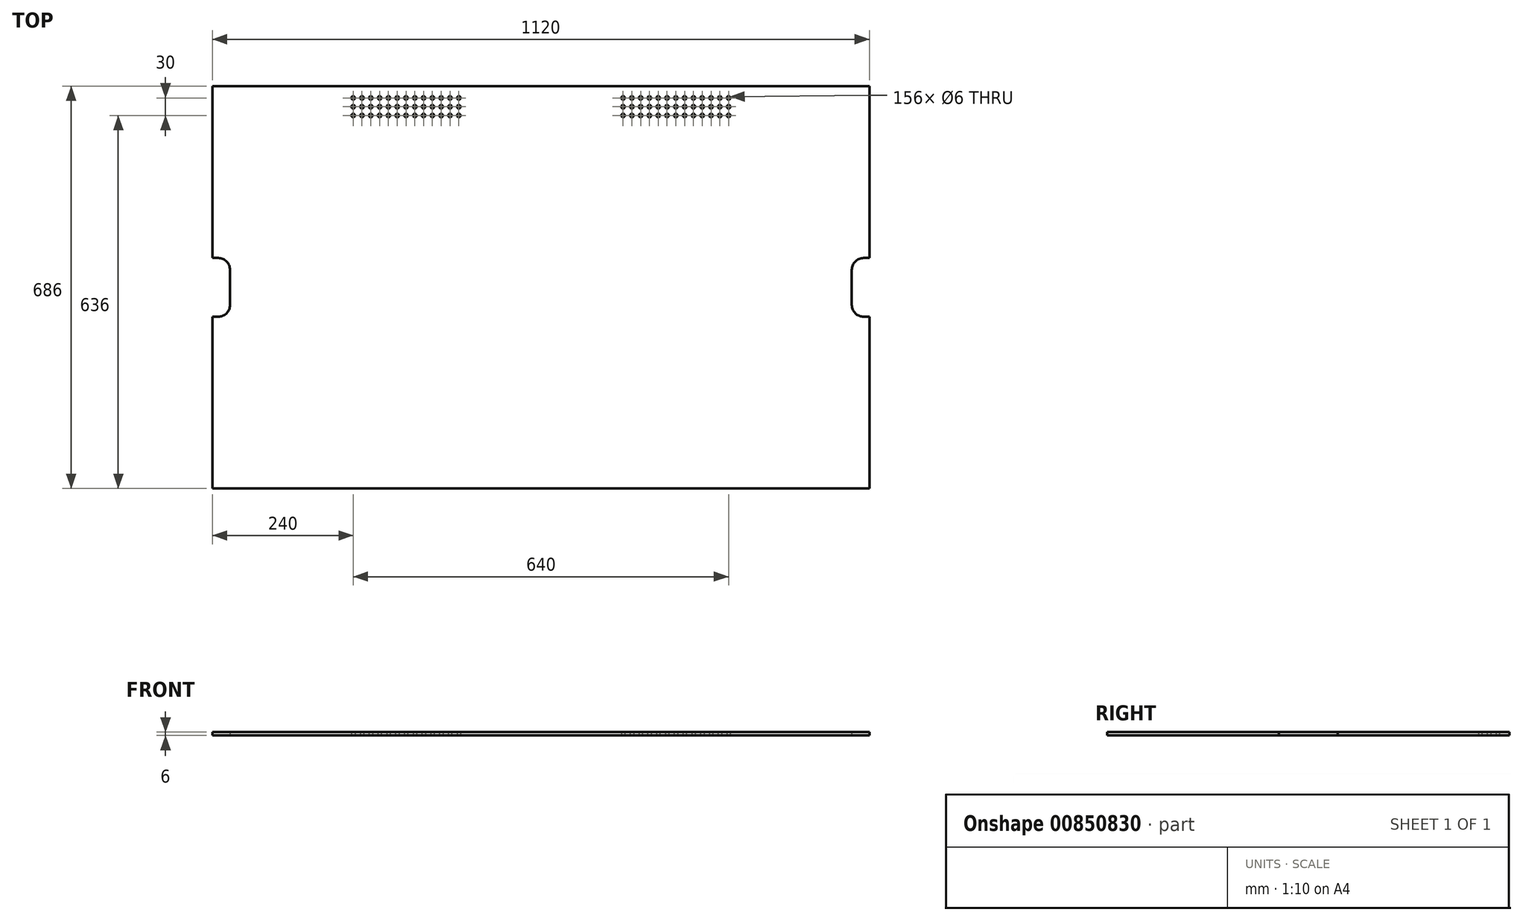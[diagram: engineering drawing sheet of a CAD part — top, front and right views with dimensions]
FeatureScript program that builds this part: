
annotation { "Feature Type Name" : "Feature", "Feature Type Description" : "" }
export const myFeature = defineFeature(function(context is Context, id is Id, definition is map)
    precondition{}
    {
        {
            var Q0;
            Q0=qCreatedBy(makeId("Top.planeOp"),FACE);
            var sketch = newSketch(context, id + "F0", { "sketchPlane" : qUnion([Q0])});
            skLineSegment(sketch, "E0", {"start": v(-560, 343) * mm, "end": v(-560, 50) * mm});
            skLineSegment(sketch, "E1", {"start": v(-560, 50) * mm, "end": v(-550, 50) * mm});
            skArc(sketch, "E2", {"start": v(-550, 50) * mm, "mid": v(-535.86, 44.14) * mm, "end": v(-530, 30) * mm});
            skLineSegment(sketch, "E3", {"start": v(-530, 30) * mm, "end": v(-530, -30) * mm});
            skArc(sketch, "E4", {"start": v(-530, -30) * mm, "mid": v(-535.86, -44.14) * mm, "end": v(-550, -50) * mm});
            skLineSegment(sketch, "E5", {"start": v(-550, -50) * mm, "end": v(-560, -50) * mm});
            skLineSegment(sketch, "E6", {"start": v(-560, -50) * mm, "end": v(-560, -343) * mm});
            skCircle(sketch, "E7", {"center": v(-140, 323) * mm, "radius": 3 * mm});
            skCircle(sketch, "E8.0.1.0", {"center": v(-140, 308) * mm, "radius": 3 * mm});
            skCircle(sketch, "E8.0.2.0", {"center": v(-140, 293) * mm, "radius": 3 * mm});
            skCircle(sketch, "E8.1.0.0", {"center": v(-155, 323) * mm, "radius": 3 * mm});
            skCircle(sketch, "E8.1.1.0", {"center": v(-155, 308) * mm, "radius": 3 * mm});
            skCircle(sketch, "E8.1.2.0", {"center": v(-155, 293) * mm, "radius": 3 * mm});
            skCircle(sketch, "E8.2.0.0", {"center": v(-170, 323) * mm, "radius": 3 * mm});
            skCircle(sketch, "E8.2.1.0", {"center": v(-170, 308) * mm, "radius": 3 * mm});
            skCircle(sketch, "E8.2.2.0", {"center": v(-170, 293) * mm, "radius": 3 * mm});
            skCircle(sketch, "E8.3.0.0", {"center": v(-185, 323) * mm, "radius": 3 * mm});
            skCircle(sketch, "E8.3.1.0", {"center": v(-185, 308) * mm, "radius": 3 * mm});
            skCircle(sketch, "E8.3.2.0", {"center": v(-185, 293) * mm, "radius": 3 * mm});
            skCircle(sketch, "E8.4.0.0", {"center": v(-200, 323) * mm, "radius": 3 * mm});
            skCircle(sketch, "E8.4.1.0", {"center": v(-200, 308) * mm, "radius": 3 * mm});
            skCircle(sketch, "E8.4.2.0", {"center": v(-200, 293) * mm, "radius": 3 * mm});
            skCircle(sketch, "E8.5.0.0", {"center": v(-215, 323) * mm, "radius": 3 * mm});
            skCircle(sketch, "E8.5.1.0", {"center": v(-215, 308) * mm, "radius": 3 * mm});
            skCircle(sketch, "E8.5.2.0", {"center": v(-215, 293) * mm, "radius": 3 * mm});
            skCircle(sketch, "E8.6.0.0", {"center": v(-230, 323) * mm, "radius": 3 * mm});
            skCircle(sketch, "E8.6.1.0", {"center": v(-230, 308) * mm, "radius": 3 * mm});
            skCircle(sketch, "E8.6.2.0", {"center": v(-230, 293) * mm, "radius": 3 * mm});
            skCircle(sketch, "E8.7.0.0", {"center": v(-245, 323) * mm, "radius": 3 * mm});
            skCircle(sketch, "E8.7.1.0", {"center": v(-245, 308) * mm, "radius": 3 * mm});
            skCircle(sketch, "E8.7.2.0", {"center": v(-245, 293) * mm, "radius": 3 * mm});
            skCircle(sketch, "E8.8.0.0", {"center": v(-260, 323) * mm, "radius": 3 * mm});
            skCircle(sketch, "E8.8.1.0", {"center": v(-260, 308) * mm, "radius": 3 * mm});
            skCircle(sketch, "E8.8.2.0", {"center": v(-260, 293) * mm, "radius": 3 * mm});
            skCircle(sketch, "E8.9.0.0", {"center": v(-275, 323) * mm, "radius": 3 * mm});
            skCircle(sketch, "E8.9.1.0", {"center": v(-275, 308) * mm, "radius": 3 * mm});
            skCircle(sketch, "E8.9.2.0", {"center": v(-275, 293) * mm, "radius": 3 * mm});
            skCircle(sketch, "E8.10.0.0", {"center": v(-290, 323) * mm, "radius": 3 * mm});
            skCircle(sketch, "E8.10.1.0", {"center": v(-290, 308) * mm, "radius": 3 * mm});
            skCircle(sketch, "E8.10.2.0", {"center": v(-290, 293) * mm, "radius": 3 * mm});
            skCircle(sketch, "E8.11.0.0", {"center": v(-305, 323) * mm, "radius": 3 * mm});
            skCircle(sketch, "E8.11.1.0", {"center": v(-305, 308) * mm, "radius": 3 * mm});
            skCircle(sketch, "E8.11.2.0", {"center": v(-305, 293) * mm, "radius": 3 * mm});
            skCircle(sketch, "E8.12.0.0", {"center": v(-320, 323) * mm, "radius": 3 * mm});
            skCircle(sketch, "E8.12.1.0", {"center": v(-320, 308) * mm, "radius": 3 * mm});
            skCircle(sketch, "E8.12.2.0", {"center": v(-320, 293) * mm, "radius": 3 * mm});
            skLineSegment(sketch, "E8.direction1", {"start": v(-140, 323) * mm, "end": v(-155, 323) * mm, "construction": true});
            skLineSegment(sketch, "E8.direction2", {"start": v(-140, 323) * mm, "end": v(-140, 308) * mm, "construction": true});
            skLineSegment(sketch, "E9", {"start": v(-560, 343) * mm, "end": v(0, 343) * mm});
            skLineSegment(sketch, "E10", {"start": v(-560, -343) * mm, "end": v(0, -343) * mm});
            skLineSegment(sketch, "E11", {"start": v(-612.39, 0) * mm, "end": v(606.49, 0) * mm, "construction": true});
            skLineSegment(sketch, "E12", {"start": v(0, 429.06) * mm, "end": v(0, -433.74) * mm, "construction": true});
            skLineSegment(sketch, "E13.MirrorCS", {"start": v(560, 343) * mm, "end": v(0, 343) * mm});
            skLineSegment(sketch, "E14.MirrorCS", {"start": v(560, 343) * mm, "end": v(560, 50) * mm});
            skLineSegment(sketch, "E15.MirrorCS", {"start": v(560, 50) * mm, "end": v(550, 50) * mm});
            skArc(sketch, "E16.MirrorCS", {"start": v(550, 50) * mm, "mid": v(535.86, 44.14) * mm, "end": v(530, 30) * mm});
            skLineSegment(sketch, "E17.MirrorCS", {"start": v(530, 30) * mm, "end": v(530, -30) * mm});
            skArc(sketch, "E18.MirrorCS", {"start": v(530, -30) * mm, "mid": v(535.86, -44.14) * mm, "end": v(550, -50) * mm});
            skLineSegment(sketch, "E19.MirrorCS", {"start": v(550, -50) * mm, "end": v(560, -50) * mm});
            skLineSegment(sketch, "E20.MirrorCS", {"start": v(560, -50) * mm, "end": v(560, -343) * mm});
            skLineSegment(sketch, "E21.MirrorCS", {"start": v(560, -343) * mm, "end": v(0, -343) * mm});
            skCircle(sketch, "E22.MirrorC", {"center": v(140, 323) * mm, "radius": 3 * mm});
            skCircle(sketch, "E23.MirrorC", {"center": v(155, 323) * mm, "radius": 3 * mm});
            skCircle(sketch, "E24.MirrorC", {"center": v(170, 323) * mm, "radius": 3 * mm});
            skCircle(sketch, "E25.MirrorC", {"center": v(185, 323) * mm, "radius": 3 * mm});
            skCircle(sketch, "E26.MirrorC", {"center": v(200, 323) * mm, "radius": 3 * mm});
            skCircle(sketch, "E27.MirrorC", {"center": v(215, 323) * mm, "radius": 3 * mm});
            skCircle(sketch, "E28.MirrorC", {"center": v(230, 323) * mm, "radius": 3 * mm});
            skCircle(sketch, "E29.MirrorC", {"center": v(245, 323) * mm, "radius": 3 * mm});
            skCircle(sketch, "E30.MirrorC", {"center": v(260, 323) * mm, "radius": 3 * mm});
            skCircle(sketch, "E31.MirrorC", {"center": v(275, 323) * mm, "radius": 3 * mm});
            skCircle(sketch, "E32.MirrorC", {"center": v(290, 323) * mm, "radius": 3 * mm});
            skCircle(sketch, "E33.MirrorC", {"center": v(305, 323) * mm, "radius": 3 * mm});
            skCircle(sketch, "E34.MirrorC", {"center": v(320, 323) * mm, "radius": 3 * mm});
            skCircle(sketch, "E35.MirrorC", {"center": v(320, 308) * mm, "radius": 3 * mm});
            skCircle(sketch, "E36.MirrorC", {"center": v(305, 308) * mm, "radius": 3 * mm});
            skCircle(sketch, "E37.MirrorC", {"center": v(290, 308) * mm, "radius": 3 * mm});
            skCircle(sketch, "E38.MirrorC", {"center": v(275, 308) * mm, "radius": 3 * mm});
            skCircle(sketch, "E39.MirrorC", {"center": v(260, 308) * mm, "radius": 3 * mm});
            skCircle(sketch, "E40.MirrorC", {"center": v(245, 308) * mm, "radius": 3 * mm});
            skCircle(sketch, "E41.MirrorC", {"center": v(230, 308) * mm, "radius": 3 * mm});
            skCircle(sketch, "E42.MirrorC", {"center": v(215, 308) * mm, "radius": 3 * mm});
            skCircle(sketch, "E43.MirrorC", {"center": v(200, 308) * mm, "radius": 3 * mm});
            skCircle(sketch, "E44.MirrorC", {"center": v(185, 308) * mm, "radius": 3 * mm});
            skCircle(sketch, "E45.MirrorC", {"center": v(170, 308) * mm, "radius": 3 * mm});
            skCircle(sketch, "E46.MirrorC", {"center": v(155, 308) * mm, "radius": 3 * mm});
            skCircle(sketch, "E47.MirrorC", {"center": v(140, 308) * mm, "radius": 3 * mm});
            skCircle(sketch, "E48.MirrorC", {"center": v(140, 293) * mm, "radius": 3 * mm});
            skCircle(sketch, "E49.MirrorC", {"center": v(155, 293) * mm, "radius": 3 * mm});
            skCircle(sketch, "E50.MirrorC", {"center": v(170, 293) * mm, "radius": 3 * mm});
            skCircle(sketch, "E51.MirrorC", {"center": v(185, 293) * mm, "radius": 3 * mm});
            skCircle(sketch, "E52.MirrorC", {"center": v(200, 293) * mm, "radius": 3 * mm});
            skCircle(sketch, "E53.MirrorC", {"center": v(215, 293) * mm, "radius": 3 * mm});
            skCircle(sketch, "E54.MirrorC", {"center": v(230, 293) * mm, "radius": 3 * mm});
            skCircle(sketch, "E55.MirrorC", {"center": v(245, 293) * mm, "radius": 3 * mm});
            skCircle(sketch, "E56.MirrorC", {"center": v(260, 293) * mm, "radius": 3 * mm});
            skCircle(sketch, "E57.MirrorC", {"center": v(275, 293) * mm, "radius": 3 * mm});
            skCircle(sketch, "E58.MirrorC", {"center": v(290, 293) * mm, "radius": 3 * mm});
            skCircle(sketch, "E59.MirrorC", {"center": v(305, 293) * mm, "radius": 3 * mm});
            skCircle(sketch, "E60.MirrorC", {"center": v(320, 293) * mm, "radius": 3 * mm});
            skSolve(sketch);
        }
        {
            var Q0;
            Q0=makeQuery(id+"F0.imprint","IMPRINT",FACE,{"disambiguationData":[TD([[makeQuery(id+"F0.imprint","IMPRINT",EDGE,{"derivedFrom":sQuery(id+"F0.wireOp",EDGE,"E0")}),1.0]])]});
            extrude(context, id + "F1", {"entities" : qUnion([Q0]), "depth" : 6 * mm, "offsetDistance" : 25 * mm});
        }
        {
            var Q0;
            Q0=makeQuery(id+"F1.opExtrude","SWEPT_BODY",BODY,{"disambiguationData":[OSD([sQuery(id+"F0.wireOp",EDGE,"E0"),sQuery(id+"F0.wireOp",EDGE,"E1"),sQuery(id+"F0.wireOp",EDGE,"E2"),sQuery(id+"F0.wireOp",EDGE,"E3"),sQuery(id+"F0.wireOp",EDGE,"E4"),sQuery(id+"F0.wireOp",EDGE,"E5"),sQuery(id+"F0.wireOp",EDGE,"E6"),sQuery(id+"F0.wireOp",EDGE,"E7"),sQuery(id+"F0.wireOp",EDGE,"E8.0.1.0"),sQuery(id+"F0.wireOp",EDGE,"E8.0.2.0"),sQuery(id+"F0.wireOp",EDGE,"E8.1.0.0"),sQuery(id+"F0.wireOp",EDGE,"E8.1.1.0"),sQuery(id+"F0.wireOp",EDGE,"E8.1.2.0"),sQuery(id+"F0.wireOp",EDGE,"E8.2.0.0"),sQuery(id+"F0.wireOp",EDGE,"E8.2.1.0"),sQuery(id+"F0.wireOp",EDGE,"E8.2.2.0"),sQuery(id+"F0.wireOp",EDGE,"E8.3.0.0"),sQuery(id+"F0.wireOp",EDGE,"E8.3.1.0"),sQuery(id+"F0.wireOp",EDGE,"E8.3.2.0"),sQuery(id+"F0.wireOp",EDGE,"E8.4.0.0"),sQuery(id+"F0.wireOp",EDGE,"E8.4.1.0"),sQuery(id+"F0.wireOp",EDGE,"E8.4.2.0"),sQuery(id+"F0.wireOp",EDGE,"E8.5.0.0"),sQuery(id+"F0.wireOp",EDGE,"E8.5.1.0"),sQuery(id+"F0.wireOp",EDGE,"E8.5.2.0"),sQuery(id+"F0.wireOp",EDGE,"E8.6.0.0"),sQuery(id+"F0.wireOp",EDGE,"E8.6.1.0"),sQuery(id+"F0.wireOp",EDGE,"E8.6.2.0"),sQuery(id+"F0.wireOp",EDGE,"E8.7.0.0"),sQuery(id+"F0.wireOp",EDGE,"E8.7.1.0"),sQuery(id+"F0.wireOp",EDGE,"E8.7.2.0"),sQuery(id+"F0.wireOp",EDGE,"E8.8.0.0"),sQuery(id+"F0.wireOp",EDGE,"E8.8.1.0"),sQuery(id+"F0.wireOp",EDGE,"E8.8.2.0"),sQuery(id+"F0.wireOp",EDGE,"E8.9.0.0"),sQuery(id+"F0.wireOp",EDGE,"E8.9.1.0"),sQuery(id+"F0.wireOp",EDGE,"E8.9.2.0"),sQuery(id+"F0.wireOp",EDGE,"E8.10.0.0"),sQuery(id+"F0.wireOp",EDGE,"E8.10.1.0"),sQuery(id+"F0.wireOp",EDGE,"E8.10.2.0"),sQuery(id+"F0.wireOp",EDGE,"E8.11.0.0"),sQuery(id+"F0.wireOp",EDGE,"E8.11.1.0"),sQuery(id+"F0.wireOp",EDGE,"E8.11.2.0"),sQuery(id+"F0.wireOp",EDGE,"E8.12.0.0"),sQuery(id+"F0.wireOp",EDGE,"E8.12.1.0"),sQuery(id+"F0.wireOp",EDGE,"E8.12.2.0"),sQuery(id+"F0.wireOp",EDGE,"E9"),sQuery(id+"F0.wireOp",EDGE,"E10"),sQuery(id+"F0.wireOp",EDGE,"E13.MirrorCS"),sQuery(id+"F0.wireOp",EDGE,"E14.MirrorCS"),sQuery(id+"F0.wireOp",EDGE,"E15.MirrorCS"),sQuery(id+"F0.wireOp",EDGE,"E16.MirrorCS"),sQuery(id+"F0.wireOp",EDGE,"E17.MirrorCS"),sQuery(id+"F0.wireOp",EDGE,"E18.MirrorCS"),sQuery(id+"F0.wireOp",EDGE,"E19.MirrorCS"),sQuery(id+"F0.wireOp",EDGE,"E20.MirrorCS"),sQuery(id+"F0.wireOp",EDGE,"E21.MirrorCS"),sQuery(id+"F0.wireOp",EDGE,"E22.MirrorC"),sQuery(id+"F0.wireOp",EDGE,"E23.MirrorC"),sQuery(id+"F0.wireOp",EDGE,"E24.MirrorC"),sQuery(id+"F0.wireOp",EDGE,"E25.MirrorC"),sQuery(id+"F0.wireOp",EDGE,"E26.MirrorC"),sQuery(id+"F0.wireOp",EDGE,"E27.MirrorC"),sQuery(id+"F0.wireOp",EDGE,"E28.MirrorC"),sQuery(id+"F0.wireOp",EDGE,"E29.MirrorC"),sQuery(id+"F0.wireOp",EDGE,"E30.MirrorC"),sQuery(id+"F0.wireOp",EDGE,"E31.MirrorC"),sQuery(id+"F0.wireOp",EDGE,"E32.MirrorC"),sQuery(id+"F0.wireOp",EDGE,"E33.MirrorC"),sQuery(id+"F0.wireOp",EDGE,"E34.MirrorC"),sQuery(id+"F0.wireOp",EDGE,"E35.MirrorC"),sQuery(id+"F0.wireOp",EDGE,"E36.MirrorC"),sQuery(id+"F0.wireOp",EDGE,"E37.MirrorC"),sQuery(id+"F0.wireOp",EDGE,"E38.MirrorC"),sQuery(id+"F0.wireOp",EDGE,"E39.MirrorC"),sQuery(id+"F0.wireOp",EDGE,"E40.MirrorC"),sQuery(id+"F0.wireOp",EDGE,"E41.MirrorC"),sQuery(id+"F0.wireOp",EDGE,"E42.MirrorC"),sQuery(id+"F0.wireOp",EDGE,"E43.MirrorC"),sQuery(id+"F0.wireOp",EDGE,"E44.MirrorC"),sQuery(id+"F0.wireOp",EDGE,"E45.MirrorC"),sQuery(id+"F0.wireOp",EDGE,"E46.MirrorC"),sQuery(id+"F0.wireOp",EDGE,"E47.MirrorC"),sQuery(id+"F0.wireOp",EDGE,"E48.MirrorC"),sQuery(id+"F0.wireOp",EDGE,"E49.MirrorC"),sQuery(id+"F0.wireOp",EDGE,"E50.MirrorC"),sQuery(id+"F0.wireOp",EDGE,"E51.MirrorC"),sQuery(id+"F0.wireOp",EDGE,"E52.MirrorC"),sQuery(id+"F0.wireOp",EDGE,"E53.MirrorC"),sQuery(id+"F0.wireOp",EDGE,"E54.MirrorC"),sQuery(id+"F0.wireOp",EDGE,"E55.MirrorC"),sQuery(id+"F0.wireOp",EDGE,"E56.MirrorC"),sQuery(id+"F0.wireOp",EDGE,"E57.MirrorC"),sQuery(id+"F0.wireOp",EDGE,"E58.MirrorC"),sQuery(id+"F0.wireOp",EDGE,"E59.MirrorC"),sQuery(id+"F0.wireOp",EDGE,"E60.MirrorC")])]});
            transform(context, id + "F2", {"entities" : qUnion([Q0]), "transformType" : TransformType.TRANSLATION_3D, "dx" : 0 * mm, "dy" : 0 * mm, "dz" : 0 * mm, "makeCopy" : true});
        }
        {
            var Q0;
            Q0=makeQuery(id+"F2.opPattern","COPY",FACE,{"derivedFrom":makeQuery(id+"F1.opExtrude","CAP_FACE",FACE,{"disambiguationData":[OSD([sQuery(id+"F0.wireOp",EDGE,"E0"),sQuery(id+"F0.wireOp",EDGE,"E1"),sQuery(id+"F0.wireOp",EDGE,"E2"),sQuery(id+"F0.wireOp",EDGE,"E3"),sQuery(id+"F0.wireOp",EDGE,"E4"),sQuery(id+"F0.wireOp",EDGE,"E5"),sQuery(id+"F0.wireOp",EDGE,"E6"),sQuery(id+"F0.wireOp",EDGE,"E7"),sQuery(id+"F0.wireOp",EDGE,"E8.0.1.0"),sQuery(id+"F0.wireOp",EDGE,"E8.0.2.0"),sQuery(id+"F0.wireOp",EDGE,"E8.1.0.0"),sQuery(id+"F0.wireOp",EDGE,"E8.1.1.0"),sQuery(id+"F0.wireOp",EDGE,"E8.1.2.0"),sQuery(id+"F0.wireOp",EDGE,"E8.2.0.0"),sQuery(id+"F0.wireOp",EDGE,"E8.2.1.0"),sQuery(id+"F0.wireOp",EDGE,"E8.2.2.0"),sQuery(id+"F0.wireOp",EDGE,"E8.3.0.0"),sQuery(id+"F0.wireOp",EDGE,"E8.3.1.0"),sQuery(id+"F0.wireOp",EDGE,"E8.3.2.0"),sQuery(id+"F0.wireOp",EDGE,"E8.4.0.0"),sQuery(id+"F0.wireOp",EDGE,"E8.4.1.0"),sQuery(id+"F0.wireOp",EDGE,"E8.4.2.0"),sQuery(id+"F0.wireOp",EDGE,"E8.5.0.0"),sQuery(id+"F0.wireOp",EDGE,"E8.5.1.0"),sQuery(id+"F0.wireOp",EDGE,"E8.5.2.0"),sQuery(id+"F0.wireOp",EDGE,"E8.6.0.0"),sQuery(id+"F0.wireOp",EDGE,"E8.6.1.0"),sQuery(id+"F0.wireOp",EDGE,"E8.6.2.0"),sQuery(id+"F0.wireOp",EDGE,"E8.7.0.0"),sQuery(id+"F0.wireOp",EDGE,"E8.7.1.0"),sQuery(id+"F0.wireOp",EDGE,"E8.7.2.0"),sQuery(id+"F0.wireOp",EDGE,"E8.8.0.0"),sQuery(id+"F0.wireOp",EDGE,"E8.8.1.0"),sQuery(id+"F0.wireOp",EDGE,"E8.8.2.0"),sQuery(id+"F0.wireOp",EDGE,"E8.9.0.0"),sQuery(id+"F0.wireOp",EDGE,"E8.9.1.0"),sQuery(id+"F0.wireOp",EDGE,"E8.9.2.0"),sQuery(id+"F0.wireOp",EDGE,"E8.10.0.0"),sQuery(id+"F0.wireOp",EDGE,"E8.10.1.0"),sQuery(id+"F0.wireOp",EDGE,"E8.10.2.0"),sQuery(id+"F0.wireOp",EDGE,"E8.11.0.0"),sQuery(id+"F0.wireOp",EDGE,"E8.11.1.0"),sQuery(id+"F0.wireOp",EDGE,"E8.11.2.0"),sQuery(id+"F0.wireOp",EDGE,"E8.12.0.0"),sQuery(id+"F0.wireOp",EDGE,"E8.12.1.0"),sQuery(id+"F0.wireOp",EDGE,"E8.12.2.0"),sQuery(id+"F0.wireOp",EDGE,"E9"),sQuery(id+"F0.wireOp",EDGE,"E10"),sQuery(id+"F0.wireOp",EDGE,"E13.MirrorCS"),sQuery(id+"F0.wireOp",EDGE,"E14.MirrorCS"),sQuery(id+"F0.wireOp",EDGE,"E15.MirrorCS"),sQuery(id+"F0.wireOp",EDGE,"E16.MirrorCS"),sQuery(id+"F0.wireOp",EDGE,"E17.MirrorCS"),sQuery(id+"F0.wireOp",EDGE,"E18.MirrorCS"),sQuery(id+"F0.wireOp",EDGE,"E19.MirrorCS"),sQuery(id+"F0.wireOp",EDGE,"E20.MirrorCS"),sQuery(id+"F0.wireOp",EDGE,"E21.MirrorCS"),sQuery(id+"F0.wireOp",EDGE,"E22.MirrorC"),sQuery(id+"F0.wireOp",EDGE,"E23.MirrorC"),sQuery(id+"F0.wireOp",EDGE,"E24.MirrorC"),sQuery(id+"F0.wireOp",EDGE,"E25.MirrorC"),sQuery(id+"F0.wireOp",EDGE,"E26.MirrorC"),sQuery(id+"F0.wireOp",EDGE,"E27.MirrorC"),sQuery(id+"F0.wireOp",EDGE,"E28.MirrorC"),sQuery(id+"F0.wireOp",EDGE,"E29.MirrorC"),sQuery(id+"F0.wireOp",EDGE,"E30.MirrorC"),sQuery(id+"F0.wireOp",EDGE,"E31.MirrorC"),sQuery(id+"F0.wireOp",EDGE,"E32.MirrorC"),sQuery(id+"F0.wireOp",EDGE,"E33.MirrorC"),sQuery(id+"F0.wireOp",EDGE,"E34.MirrorC"),sQuery(id+"F0.wireOp",EDGE,"E35.MirrorC"),sQuery(id+"F0.wireOp",EDGE,"E36.MirrorC"),sQuery(id+"F0.wireOp",EDGE,"E37.MirrorC"),sQuery(id+"F0.wireOp",EDGE,"E38.MirrorC"),sQuery(id+"F0.wireOp",EDGE,"E39.MirrorC"),sQuery(id+"F0.wireOp",EDGE,"E40.MirrorC"),sQuery(id+"F0.wireOp",EDGE,"E41.MirrorC"),sQuery(id+"F0.wireOp",EDGE,"E42.MirrorC"),sQuery(id+"F0.wireOp",EDGE,"E43.MirrorC"),sQuery(id+"F0.wireOp",EDGE,"E44.MirrorC"),sQuery(id+"F0.wireOp",EDGE,"E45.MirrorC"),sQuery(id+"F0.wireOp",EDGE,"E46.MirrorC"),sQuery(id+"F0.wireOp",EDGE,"E47.MirrorC"),sQuery(id+"F0.wireOp",EDGE,"E48.MirrorC"),sQuery(id+"F0.wireOp",EDGE,"E49.MirrorC"),sQuery(id+"F0.wireOp",EDGE,"E50.MirrorC"),sQuery(id+"F0.wireOp",EDGE,"E51.MirrorC"),sQuery(id+"F0.wireOp",EDGE,"E52.MirrorC"),sQuery(id+"F0.wireOp",EDGE,"E53.MirrorC"),sQuery(id+"F0.wireOp",EDGE,"E54.MirrorC"),sQuery(id+"F0.wireOp",EDGE,"E55.MirrorC"),sQuery(id+"F0.wireOp",EDGE,"E56.MirrorC"),sQuery(id+"F0.wireOp",EDGE,"E57.MirrorC"),sQuery(id+"F0.wireOp",EDGE,"E58.MirrorC"),sQuery(id+"F0.wireOp",EDGE,"E59.MirrorC"),sQuery(id+"F0.wireOp",EDGE,"E60.MirrorC")])],"isStart":false}),"instanceName":"1"});
            cPlane(context, id + "F3", {"entities" : qUnion([Q0]), "cplaneType" : CPlaneType.OFFSET, "offset" : 25 * mm, "width" : 150 * mm, "height" : 150 * mm});
        }
    });
